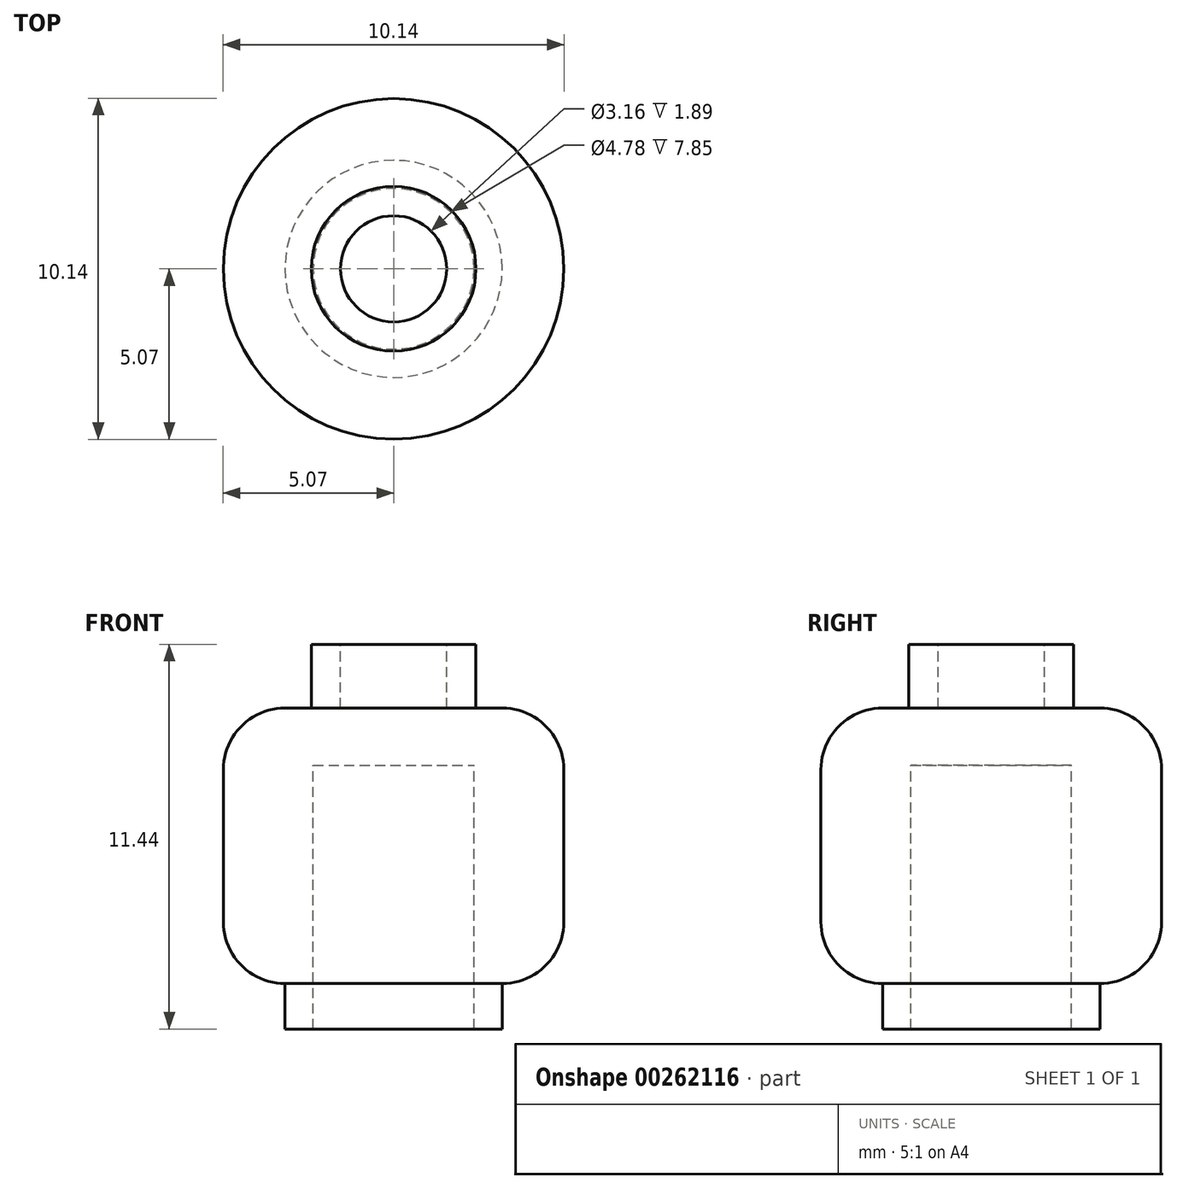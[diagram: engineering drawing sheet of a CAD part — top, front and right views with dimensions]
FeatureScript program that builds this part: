
annotation { "Feature Type Name" : "Feature", "Feature Type Description" : "" }
export const myFeature = defineFeature(function(context is Context, id is Id, definition is map)
    precondition{}
    {
        {
            var Q0;
            Q0=qCreatedBy(makeId("Top.planeOp"),FACE);
            var sketch = newSketch(context, id + "F0", { "sketchPlane" : qUnion([Q0])});
            skCircle(sketch, "E0", {"center": v(0, 0) * mm, "radius": 5.07 * mm});
            skSolve(sketch);
        }
        {
            var Q0;
            Q0=makeQuery(id+"F0.imprint","IMPRINT",FACE,{"disambiguationData":[TD([[makeQuery(id+"F0.imprint","IMPRINT",EDGE,{"derivedFrom":sQuery(id+"F0.wireOp",EDGE,"E0")}),1.0]])]});
            extrude(context, id + "F1", {"entities" : qUnion([Q0]), "depth" : 8.2 * mm});
        }
        {
            var Q0;
            Q0=makeQuery(id+"F1.opExtrude","CAP_EDGE",EDGE,{"disambiguationData":[OSD([sQuery(id+"F0.wireOp",EDGE,"E0")])],"isStart":false});
            var Q1;
            Q1=makeQuery(id+"F1.opExtrude","CAP_EDGE",EDGE,{"disambiguationData":[OSD([sQuery(id+"F0.wireOp",EDGE,"E0")])],"isStart":true});
            fillet(context, id + "F2", {"entities" : qUnion([Q0, Q1]), "radius" : 1.83 * mm, "tangentPropagation" : true, "allowEdgeOverflow" : false});
        }
        {
            var Q0;
            Q0=makeQuery(id+"F1.opExtrude","CAP_FACE",FACE,{"disambiguationData":[OSD([sQuery(id+"F0.wireOp",EDGE,"E0")])],"isStart":false});
            var sketch = newSketch(context, id + "F3", { "sketchPlane" : qUnion([Q0])});
            skCircle(sketch, "E1", {"center": v(0, 0) * mm, "radius": 2.45 * mm});
            skSolve(sketch);
        }
        {
            var Q0;
            Q0=makeQuery(id+"F3.imprint","IMPRINT",FACE,{"disambiguationData":[TD([[makeQuery(id+"F3.imprint","IMPRINT",EDGE,{"derivedFrom":sQuery(id+"F3.wireOp",EDGE,"E1")}),1.0]])]});
            extrude(context, id + "F4", {"entities" : qUnion([Q0]), "operationType" : NewBodyOperationType.ADD, "depth" : 1.89 * mm});
        }
        {
            var Q0;
            Q0=makeQuery(id+"F4.opExtrude","CAP_FACE",FACE,{"disambiguationData":[OSD([sQuery(id+"F3.wireOp",EDGE,"E1")])],"isStart":false});
            var sketch = newSketch(context, id + "F5", { "sketchPlane" : qUnion([Q0])});
            skCircle(sketch, "E2.0", {"center": v(0, 0) * mm, "radius": 1.58 * mm});
            skSolve(sketch);
        }
        {
            var Q0;
            Q0=makeQuery(id+"F5.imprint","IMPRINT",FACE,{"disambiguationData":[TD([[makeQuery(id+"F5.imprint","IMPRINT",EDGE,{"derivedFrom":sQuery(id+"F5.wireOp",EDGE,"E2.0")}),1.0]])]});
            extrude(context, id + "F6", {"entities" : qUnion([Q0]), "operationType" : NewBodyOperationType.REMOVE, "oppositeDirection" : true, "depth" : 1.89 * mm});
        }
        {
            var Q0;
            Q0=makeQuery(id+"F1.opExtrude","CAP_FACE",FACE,{"disambiguationData":[OSD([sQuery(id+"F0.wireOp",EDGE,"E0")])],"isStart":true});
            var sketch = newSketch(context, id + "F7", { "sketchPlane" : qUnion([Q0])});
            skCircle(sketch, "E3", {"center": v(0, 0) * mm, "radius": 3.23 * mm});
            skCircle(sketch, "E4.0", {"center": v(0, 0) * mm, "radius": 2.4 * mm});
            skSolve(sketch);
        }
        {
            var Q0;
            Q0=makeQuery(id+"F7.imprint","IMPRINT",FACE,{"disambiguationData":[TD([[makeQuery(id+"F7.imprint","IMPRINT",EDGE,{"derivedFrom":sQuery(id+"F7.wireOp",EDGE,"E4.0")}),-1.0]])]});
            extrude(context, id + "F8", {"entities" : qUnion([Q0]), "operationType" : NewBodyOperationType.ADD, "depth" : 1.35 * mm});
        }
        {
            var Q0;
            Q0=makeQuery(id+"F1.opExtrude","CAP_FACE",FACE,{"disambiguationData":[OSD([sQuery(id+"F0.wireOp",EDGE,"E0")])],"isStart":true});
            extrude(context, id + "F9", {"entities" : qUnion([Q0]), "operationType" : NewBodyOperationType.REMOVE, "oppositeDirection" : true, "depth" : 6.5 * mm});
        }
    });
